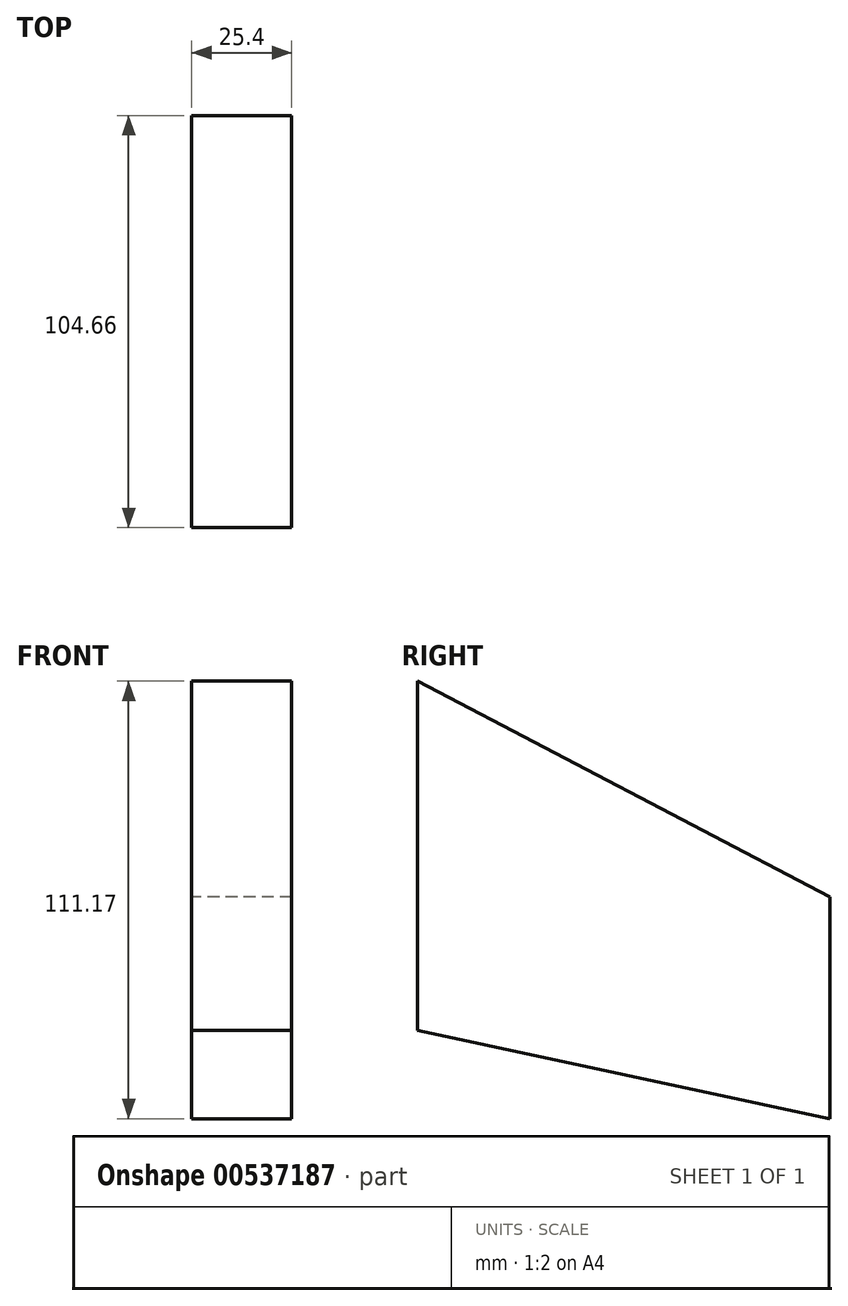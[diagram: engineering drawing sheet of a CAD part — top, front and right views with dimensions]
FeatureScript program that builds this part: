
annotation { "Feature Type Name" : "Feature", "Feature Type Description" : "" }
export const myFeature = defineFeature(function(context is Context, id is Id, definition is map)
    precondition{}
    {
        {
            var Q0;
            Q0=qCreatedBy(makeId("Right.planeOp"),FACE);
            var sketch = newSketch(context, id + "F0", { "sketchPlane" : qUnion([Q0])});
            skLineSegment(sketch, "E0", {"start": v(-104.66, 75.39) * mm, "end": v(0, 20.6) * mm});
            skLineSegment(sketch, "E1", {"start": v(0, 20.6) * mm, "end": v(0, -35.78) * mm});
            skLineSegment(sketch, "E2", {"start": v(-104.66, 75.39) * mm, "end": v(-104.66, 20.6) * mm});
            skLineSegment(sketch, "E3", {"start": v(-104.66, 20.6) * mm, "end": v(-104.66, -13.37) * mm});
            skLineSegment(sketch, "E4", {"start": v(-104.66, -13.37) * mm, "end": v(0, -35.78) * mm});
            skLineSegment(sketch, "E5", {"start": v(-104.66, 75.39) * mm, "end": v(29.57, 45.56) * mm});
            skLineSegment(sketch, "E6", {"start": v(29.57, 45.56) * mm, "end": v(0, 20.6) * mm});
            skLineSegment(sketch, "E7", {"start": v(29.57, 39.84) * mm, "end": v(11.84, -35.78) * mm});
            skLineSegment(sketch, "E8", {"start": v(11.84, -35.78) * mm, "end": v(0, -35.78) * mm});
            skLineSegment(sketch, "E9", {"start": v(29.57, 39.84) * mm, "end": v(29.57, 45.56) * mm});
            skSolve(sketch);
        }
        {
            var Q0;
            Q0=makeQuery(id+"F0.imprint","IMPRINT",FACE,{"disambiguationData":[TD([[makeQuery(id+"F0.imprint","IMPRINT",EDGE,{"derivedFrom":sQuery(id+"F0.wireOp",EDGE,"E0")}),-1.0]])]});
            extrude(context, id + "F1", {"entities" : qUnion([Q0]), "depth" : 25.4 * mm, "offsetDistance" : 25.4 * mm});
        }
    });
